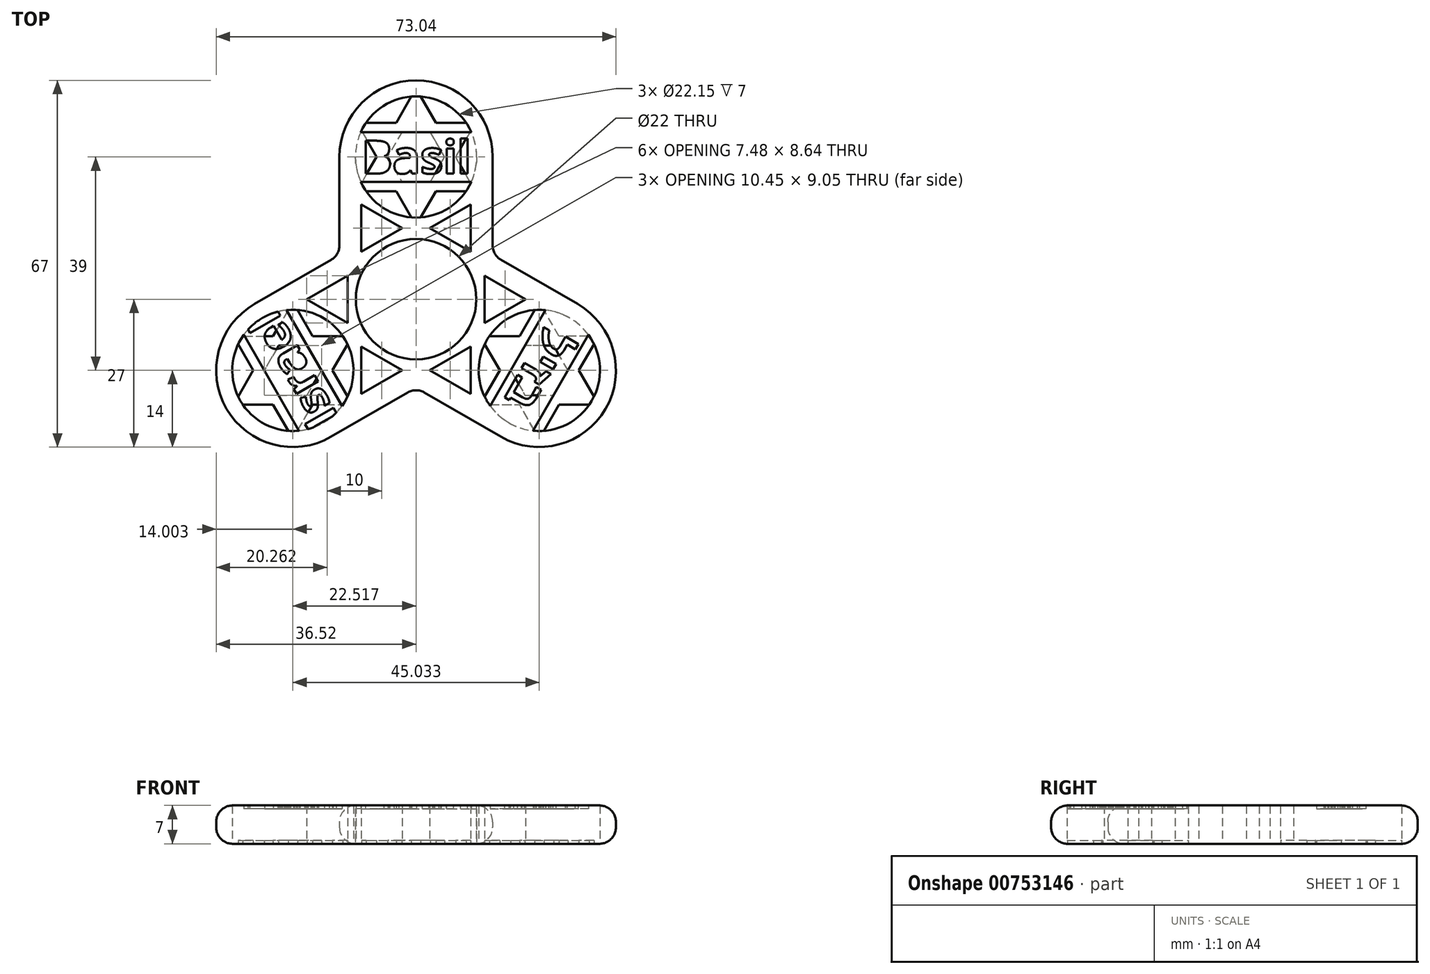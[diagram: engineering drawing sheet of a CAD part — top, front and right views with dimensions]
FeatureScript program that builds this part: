
annotation { "Feature Type Name" : "Feature", "Feature Type Description" : "" }
export const myFeature = defineFeature(function(context is Context, id is Id, definition is map)
    precondition{}
    {
        {
            var Q0;
            Q0=qCreatedBy(makeId("Top.planeOp"),FACE);
            var sketch = newSketch(context, id + "F0", { "sketchPlane" : qUnion([Q0])});
            skCircle(sketch, "E0", {"center": v(0, 0) * mm, "radius": 11 * mm});
            skArc(sketch, "E1", {"start": v(14, 26) * mm, "mid": v(0, 40) * mm, "end": v(-14, 26) * mm});
            skCircle(sketch, "E2.converted", {"center": v(0, 26) * mm, "radius": 11.07 * mm});
            skLineSegment(sketch, "E3", {"start": v(-14, 26) * mm, "end": v(-14, 9.81) * mm});
            skLineSegment(sketch, "E4", {"start": v(14, 26) * mm, "end": v(14, 9.81) * mm});
            skLineSegment(sketch, "E5.0", {"start": v(10, 17.32) * mm, "end": v(10, 8.68) * mm});
            skLineSegment(sketch, "E6", {"start": v(0, 0) * mm, "end": v(14, 8.08) * mm, "construction": true});
            skLineSegment(sketch, "E7", {"start": v(0, 0) * mm, "end": v(0, 26) * mm, "construction": true});
            skLineSegment(sketch, "E8", {"start": v(10, 17.32) * mm, "end": v(2.52, 13) * mm});
            skLineSegment(sketch, "E9", {"start": v(10, 8.68) * mm, "end": v(2.52, 13) * mm});
            skLineSegment(sketch, "E10.anchor1", {"start": v(0, 0) * mm, "end": v(10, 8.68) * mm, "construction": true});
            skPoint(sketch, "E11.visualSharp", {"position": v(14, 8.08) * mm});
            skArc(sketch, "E11.filletArc", {"start": v(14, 9.81) * mm, "mid": v(14.4, 8.31) * mm, "end": v(15.5, 7.22) * mm});
            skLineSegment(sketch, "E12", {"start": v(14, 9.81) * mm, "end": v(17, 9.81) * mm, "construction": true});
            skLineSegment(sketch, "E13", {"start": v(17, 9.81) * mm, "end": v(15.5, 7.22) * mm, "construction": true});
            skArc(sketch, "E14", {"start": v(10, 17.32) * mm, "mid": v(9.28, 13) * mm, "end": v(10, 8.68) * mm, "construction": true});
            skArc(sketch, "E15", {"start": v(2.52, 13) * mm, "mid": v(6.62, 14.53) * mm, "end": v(10, 17.32) * mm, "construction": true});
            skArc(sketch, "E16", {"start": v(10, 17.32) * mm, "mid": v(-6.62, 37.47) * mm, "end": v(2.52, 13) * mm, "construction": true});
            skArc(sketch, "E17", {"start": v(2.52, 13) * mm, "mid": v(-6.62, -11.47) * mm, "end": v(10, 8.68) * mm, "construction": true});
            skArc(sketch, "E18", {"start": v(10, 8.68) * mm, "mid": v(6.62, 11.47) * mm, "end": v(2.52, 13) * mm, "construction": true});
            skLineSegment(sketch, "E19.1.0", {"start": v(-2.52, 13) * mm, "end": v(-10, 8.68) * mm});
            skLineSegment(sketch, "E19.1.1", {"start": v(-10, 17.32) * mm, "end": v(-2.52, 13) * mm});
            skLineSegment(sketch, "E19.1.2", {"start": v(-10, 17.32) * mm, "end": v(-10, 8.68) * mm});
            skLineSegment(sketch, "E19.anchor1", {"start": v(0, 0) * mm, "end": v(2.52, 13) * mm, "construction": true});
            skLineSegment(sketch, "E19.anchor2", {"start": v(0, 0) * mm, "end": v(-10, 8.68) * mm, "construction": true});
            skLineSegment(sketch, "E20.1.0", {"start": v(-10, -8.68) * mm, "end": v(-2.52, -13) * mm});
            skLineSegment(sketch, "E20.1.1", {"start": v(-29.52, -0.88) * mm, "end": v(-15.5, 7.22) * mm});
            skCircle(sketch, "E20.1.2", {"center": v(-22.52, -13) * mm, "radius": 11.07 * mm});
            skArc(sketch, "E20.1.3", {"start": v(-20, 0) * mm, "mid": v(-29.14, -24.47) * mm, "end": v(-12.52, -4.32) * mm, "construction": true});
            skLineSegment(sketch, "E20.1.4", {"start": v(-20, 0) * mm, "end": v(-12.52, 4.32) * mm});
            skArc(sketch, "E20.1.5", {"start": v(-12.52, -4.32) * mm, "mid": v(-15.9, -1.53) * mm, "end": v(-20, 0) * mm, "construction": true});
            skArc(sketch, "E20.1.7", {"start": v(-29.52, -0.88) * mm, "mid": v(-34.64, -20) * mm, "end": v(-15.52, -25.12) * mm});
            skLineSegment(sketch, "E20.1.8", {"start": v(-10, -17.32) * mm, "end": v(-10, -8.68) * mm});
            skLineSegment(sketch, "E20.1.9", {"start": v(-15.5, 7.22) * mm, "end": v(-17, 9.81) * mm, "construction": true});
            skArc(sketch, "E20.1.10", {"start": v(-12.52, 4.32) * mm, "mid": v(-13.24, 0) * mm, "end": v(-12.52, -4.32) * mm, "construction": true});
            skLineSegment(sketch, "E20.1.11", {"start": v(-10, -17.32) * mm, "end": v(-2.52, -13) * mm});
            skLineSegment(sketch, "E20.1.12", {"start": v(-15.52, -25.12) * mm, "end": v(-1.5, -17.03) * mm});
            skArc(sketch, "E20.1.13", {"start": v(-20, 0) * mm, "mid": v(-15.9, 1.53) * mm, "end": v(-12.52, 4.32) * mm, "construction": true});
            skLineSegment(sketch, "E20.1.14", {"start": v(-20, 0) * mm, "end": v(-12.52, -4.32) * mm});
            skPoint(sketch, "E20.1.15", {"position": v(-14, 8.08) * mm});
            skLineSegment(sketch, "E20.1.16", {"start": v(-17, 9.81) * mm, "end": v(-14, 9.81) * mm, "construction": true});
            skLineSegment(sketch, "E20.1.17", {"start": v(-12.52, 4.32) * mm, "end": v(-12.52, -4.32) * mm});
            skArc(sketch, "E20.1.18", {"start": v(-15.5, 7.22) * mm, "mid": v(-14.4, 8.31) * mm, "end": v(-14, 9.81) * mm});
            skLineSegment(sketch, "E20.1.22", {"start": v(0, 0) * mm, "end": v(-12.52, 4.32) * mm, "construction": true});
            skLineSegment(sketch, "E20.1.23", {"start": v(0, 0) * mm, "end": v(-2.52, -13) * mm, "construction": true});
            skLineSegment(sketch, "E20.1.24", {"start": v(0, 0) * mm, "end": v(-12.52, -4.32) * mm, "construction": true});
            skLineSegment(sketch, "E20.1.25", {"start": v(0, 0) * mm, "end": v(-14, 8.08) * mm, "construction": true});
            skLineSegment(sketch, "E20.2.0", {"start": v(12.52, -4.32) * mm, "end": v(12.52, 4.32) * mm});
            skLineSegment(sketch, "E20.2.1", {"start": v(15.52, -25.12) * mm, "end": v(1.5, -17.03) * mm});
            skCircle(sketch, "E20.2.2", {"center": v(22.52, -13) * mm, "radius": 11.07 * mm});
            skArc(sketch, "E20.2.3", {"start": v(10, -17.32) * mm, "mid": v(35.76, -13) * mm, "end": v(10, -8.68) * mm, "construction": true});
            skLineSegment(sketch, "E20.2.4", {"start": v(10, -17.32) * mm, "end": v(2.52, -13) * mm});
            skArc(sketch, "E20.2.5", {"start": v(10, -8.68) * mm, "mid": v(9.28, -13) * mm, "end": v(10, -17.32) * mm, "construction": true});
            skArc(sketch, "E20.2.7", {"start": v(15.52, -25.12) * mm, "mid": v(34.64, -20) * mm, "end": v(29.52, -0.88) * mm});
            skLineSegment(sketch, "E20.2.8", {"start": v(20, 0) * mm, "end": v(12.52, -4.32) * mm});
            skLineSegment(sketch, "E20.2.9", {"start": v(1.5, -17.03) * mm, "end": v(0, -19.63) * mm, "construction": true});
            skArc(sketch, "E20.2.10", {"start": v(2.52, -13) * mm, "mid": v(6.62, -11.47) * mm, "end": v(10, -8.68) * mm, "construction": true});
            skLineSegment(sketch, "E20.2.11", {"start": v(20, 0) * mm, "end": v(12.52, 4.32) * mm});
            skLineSegment(sketch, "E20.2.12", {"start": v(29.52, -0.88) * mm, "end": v(15.5, 7.22) * mm});
            skArc(sketch, "E20.2.13", {"start": v(10, -17.32) * mm, "mid": v(6.62, -14.53) * mm, "end": v(2.52, -13) * mm, "construction": true});
            skLineSegment(sketch, "E20.2.14", {"start": v(10, -17.32) * mm, "end": v(10, -8.68) * mm});
            skPoint(sketch, "E20.2.15", {"position": v(0, -16.17) * mm});
            skLineSegment(sketch, "E20.2.16", {"start": v(0, -19.63) * mm, "end": v(-1.5, -17.03) * mm, "construction": true});
            skLineSegment(sketch, "E20.2.17", {"start": v(2.52, -13) * mm, "end": v(10, -8.68) * mm});
            skArc(sketch, "E20.2.18", {"start": v(1.5, -17.03) * mm, "mid": v(0, -16.63) * mm, "end": v(-1.5, -17.03) * mm});
            skLineSegment(sketch, "E20.2.22", {"start": v(0, 0) * mm, "end": v(2.52, -13) * mm, "construction": true});
            skLineSegment(sketch, "E20.2.23", {"start": v(0, 0) * mm, "end": v(12.52, 4.32) * mm, "construction": true});
            skLineSegment(sketch, "E20.2.24", {"start": v(0, 0) * mm, "end": v(10, -8.68) * mm, "construction": true});
            skLineSegment(sketch, "E20.2.25", {"start": v(0, 0) * mm, "end": v(0, -16.17) * mm, "construction": true});
            skSolve(sketch);
        }
        {
            var Q0;
            Q0=qSketchRegion(id+"F0",true);
            extrude(context, id + "F1", {"entities" : qUnion([Q0]), "depth" : 7 * mm, "offsetDistance" : 25 * mm});
        }
        {
            var Q0;
            Q0=makeQuery(id+"F1.opExtrude","CAP_FACE",FACE,{"disambiguationData":[OSD([sQuery(id+"F0.wireOp",EDGE,"E0"),sQuery(id+"F0.wireOp",EDGE,"E1"),sQuery(id+"F0.wireOp",EDGE,"E2.converted"),sQuery(id+"F0.wireOp",EDGE,"E3"),sQuery(id+"F0.wireOp",EDGE,"E4"),sQuery(id+"F0.wireOp",EDGE,"E5.0"),sQuery(id+"F0.wireOp",EDGE,"E8"),sQuery(id+"F0.wireOp",EDGE,"E9"),sQuery(id+"F0.wireOp",EDGE,"E11.filletArc"),sQuery(id+"F0.wireOp",EDGE,"E19.1.0"),sQuery(id+"F0.wireOp",EDGE,"E19.1.1"),sQuery(id+"F0.wireOp",EDGE,"E19.1.2"),sQuery(id+"F0.wireOp",EDGE,"E20.1.0"),sQuery(id+"F0.wireOp",EDGE,"E20.1.1"),sQuery(id+"F0.wireOp",EDGE,"E20.1.2"),sQuery(id+"F0.wireOp",EDGE,"E20.1.4"),sQuery(id+"F0.wireOp",EDGE,"E20.1.7"),sQuery(id+"F0.wireOp",EDGE,"E20.1.8"),sQuery(id+"F0.wireOp",EDGE,"E20.1.11"),sQuery(id+"F0.wireOp",EDGE,"E20.1.12"),sQuery(id+"F0.wireOp",EDGE,"E20.1.14"),sQuery(id+"F0.wireOp",EDGE,"E20.1.17"),sQuery(id+"F0.wireOp",EDGE,"E20.1.18"),sQuery(id+"F0.wireOp",EDGE,"E20.2.0"),sQuery(id+"F0.wireOp",EDGE,"E20.2.1"),sQuery(id+"F0.wireOp",EDGE,"E20.2.2"),sQuery(id+"F0.wireOp",EDGE,"E20.2.4"),sQuery(id+"F0.wireOp",EDGE,"E20.2.7"),sQuery(id+"F0.wireOp",EDGE,"E20.2.8"),sQuery(id+"F0.wireOp",EDGE,"E20.2.11"),sQuery(id+"F0.wireOp",EDGE,"E20.2.12"),sQuery(id+"F0.wireOp",EDGE,"E20.2.14"),sQuery(id+"F0.wireOp",EDGE,"E20.2.17"),sQuery(id+"F0.wireOp",EDGE,"E20.2.18")])],"isStart":true});
            var sketch = newSketch(context, id + "F2", { "sketchPlane" : qUnion([Q0])});
            skCircle(sketch, "E21", {"center": v(0, -26) * mm, "radius": 12.52 * mm, "construction": true});
            skLineSegment(sketch, "E22", {"start": v(-10.84, -32.26) * mm, "end": v(-3.61, -32.26) * mm});
            skLineSegment(sketch, "E23", {"start": v(10.84, -32.26) * mm, "end": v(7.23, -26) * mm});
            skLineSegment(sketch, "E24", {"start": v(-10.84, -32.26) * mm, "end": v(-7.23, -26) * mm});
            skLineSegment(sketch, "E25", {"start": v(-10.84, -19.74) * mm, "end": v(-3.61, -19.74) * mm});
            skLineSegment(sketch, "E26", {"start": v(10.84, -19.74) * mm, "end": v(7.23, -26) * mm});
            skLineSegment(sketch, "E27", {"start": v(0, -38.52) * mm, "end": v(-3.61, -32.26) * mm});
            skCircle(sketch, "E28.cCircle", {"center": v(0, -26) * mm, "radius": 4.53 * mm, "construction": true});
            skLineSegment(sketch, "E28.0", {"start": v(-5.23, -26) * mm, "end": v(-2.61, -21.47) * mm});
            skLineSegment(sketch, "E28.1", {"start": v(-2.61, -21.47) * mm, "end": v(2.61, -21.47) * mm});
            skLineSegment(sketch, "E28.2", {"start": v(2.61, -21.47) * mm, "end": v(5.23, -26) * mm});
            skLineSegment(sketch, "E28.3", {"start": v(5.23, -26) * mm, "end": v(2.61, -30.53) * mm});
            skLineSegment(sketch, "E28.4", {"start": v(2.61, -30.53) * mm, "end": v(-2.61, -30.53) * mm});
            skLineSegment(sketch, "E28.5", {"start": v(-2.61, -30.53) * mm, "end": v(-5.23, -26) * mm});
            skPoint(sketch, "E28.0.midPoint", {"position": v(-3.92, -23.74) * mm});
            skLineSegment(sketch, "E29.trimOffspring", {"start": v(3.61, -19.74) * mm, "end": v(10.84, -19.74) * mm});
            skLineSegment(sketch, "E30.trimOffspring", {"start": v(-3.61, -19.74) * mm, "end": v(0, -13.48) * mm});
            skLineSegment(sketch, "E31.trimOffspring", {"start": v(-7.23, -26) * mm, "end": v(-10.84, -19.74) * mm});
            skLineSegment(sketch, "E32.trimOffspring", {"start": v(3.61, -32.26) * mm, "end": v(10.84, -32.26) * mm});
            skLineSegment(sketch, "E33.trimOffspring", {"start": v(3.61, -32.26) * mm, "end": v(0, -38.52) * mm});
            skLineSegment(sketch, "E34.trimOffspring", {"start": v(3.61, -19.74) * mm, "end": v(0, -13.48) * mm});
            skLineSegment(sketch, "E35.1.0", {"start": v(15.3, 13) * mm, "end": v(11.68, 19.26) * mm});
            skLineSegment(sketch, "E35.1.1", {"start": v(25.13, 17.53) * mm, "end": v(27.74, 13) * mm});
            skLineSegment(sketch, "E35.1.2", {"start": v(22.52, 25.52) * mm, "end": v(18.9, 19.26) * mm});
            skLineSegment(sketch, "E35.1.3", {"start": v(18.9, 6.74) * mm, "end": v(11.68, 6.74) * mm});
            skLineSegment(sketch, "E35.1.4", {"start": v(22.52, 0.48) * mm, "end": v(18.9, 6.74) * mm});
            skCircle(sketch, "E35.1.5", {"center": v(22.52, 13) * mm, "radius": 12.52 * mm, "construction": true});
            skLineSegment(sketch, "E35.1.6", {"start": v(26.13, 19.26) * mm, "end": v(33.36, 19.26) * mm});
            skLineSegment(sketch, "E35.1.7", {"start": v(15.3, 13) * mm, "end": v(11.68, 6.74) * mm});
            skLineSegment(sketch, "E35.1.8", {"start": v(19.9, 8.47) * mm, "end": v(17.3, 13) * mm});
            skLineSegment(sketch, "E35.1.9", {"start": v(26.13, 19.26) * mm, "end": v(22.52, 25.52) * mm});
            skLineSegment(sketch, "E35.1.10", {"start": v(11.68, 19.26) * mm, "end": v(18.9, 19.26) * mm});
            skLineSegment(sketch, "E35.1.11", {"start": v(33.36, 6.74) * mm, "end": v(29.74, 13) * mm});
            skLineSegment(sketch, "E35.1.12", {"start": v(19.9, 17.53) * mm, "end": v(25.13, 17.53) * mm});
            skLineSegment(sketch, "E35.1.13", {"start": v(33.36, 6.74) * mm, "end": v(26.13, 6.74) * mm});
            skPoint(sketch, "E35.1.14", {"position": v(22.52, 8.47) * mm});
            skLineSegment(sketch, "E35.1.15", {"start": v(26.13, 6.74) * mm, "end": v(22.52, 0.48) * mm});
            skLineSegment(sketch, "E35.1.16", {"start": v(27.74, 13) * mm, "end": v(25.13, 8.47) * mm});
            skLineSegment(sketch, "E35.1.17", {"start": v(33.36, 19.26) * mm, "end": v(29.74, 13) * mm});
            skLineSegment(sketch, "E35.1.18", {"start": v(17.3, 13) * mm, "end": v(19.9, 17.53) * mm});
            skCircle(sketch, "E35.1.19", {"center": v(22.52, 13) * mm, "radius": 4.53 * mm, "construction": true});
            skLineSegment(sketch, "E35.1.20", {"start": v(25.13, 8.47) * mm, "end": v(19.9, 8.47) * mm});
            skLineSegment(sketch, "E35.2.0", {"start": v(-18.9, 6.74) * mm, "end": v(-22.52, 0.48) * mm});
            skLineSegment(sketch, "E35.2.1", {"start": v(-27.74, 13) * mm, "end": v(-25.13, 17.53) * mm});
            skLineSegment(sketch, "E35.2.2", {"start": v(-33.36, 6.74) * mm, "end": v(-26.13, 6.74) * mm});
            skLineSegment(sketch, "E35.2.3", {"start": v(-15.3, 13) * mm, "end": v(-11.68, 6.74) * mm});
            skLineSegment(sketch, "E35.2.4", {"start": v(-11.68, 19.26) * mm, "end": v(-15.3, 13) * mm});
            skCircle(sketch, "E35.2.5", {"center": v(-22.52, 13) * mm, "radius": 12.52 * mm, "construction": true});
            skLineSegment(sketch, "E35.2.6", {"start": v(-29.74, 13) * mm, "end": v(-33.36, 19.26) * mm});
            skLineSegment(sketch, "E35.2.7", {"start": v(-18.9, 6.74) * mm, "end": v(-11.68, 6.74) * mm});
            skLineSegment(sketch, "E35.2.8", {"start": v(-17.3, 13) * mm, "end": v(-19.9, 8.47) * mm});
            skLineSegment(sketch, "E35.2.9", {"start": v(-29.74, 13) * mm, "end": v(-33.36, 6.74) * mm});
            skLineSegment(sketch, "E35.2.10", {"start": v(-22.52, 0.48) * mm, "end": v(-26.13, 6.74) * mm});
            skLineSegment(sketch, "E35.2.11", {"start": v(-22.52, 25.52) * mm, "end": v(-26.13, 19.26) * mm});
            skLineSegment(sketch, "E35.2.12", {"start": v(-25.13, 8.47) * mm, "end": v(-27.74, 13) * mm});
            skLineSegment(sketch, "E35.2.13", {"start": v(-22.52, 25.52) * mm, "end": v(-18.9, 19.26) * mm});
            skPoint(sketch, "E35.2.14", {"position": v(-18.6, 15.26) * mm});
            skLineSegment(sketch, "E35.2.15", {"start": v(-18.9, 19.26) * mm, "end": v(-11.68, 19.26) * mm});
            skLineSegment(sketch, "E35.2.16", {"start": v(-25.13, 17.53) * mm, "end": v(-19.9, 17.53) * mm});
            skLineSegment(sketch, "E35.2.17", {"start": v(-33.36, 19.26) * mm, "end": v(-26.13, 19.26) * mm});
            skLineSegment(sketch, "E35.2.18", {"start": v(-19.9, 8.47) * mm, "end": v(-25.13, 8.47) * mm});
            skCircle(sketch, "E35.2.19", {"center": v(-22.52, 13) * mm, "radius": 4.53 * mm, "construction": true});
            skLineSegment(sketch, "E35.2.20", {"start": v(-19.9, 17.53) * mm, "end": v(-17.3, 13) * mm});
            skPoint(sketch, "E35.center", {"position": v(0, 0) * mm});
            skSolve(sketch);
        }
        {
            var Q0;
            Q0 = qSketchRegion(id + "F2", true);
            extrude(context, id + "F3", {"entities" : qUnion([Q0]), "operationType" : NewBodyOperationType.ADD, "oppositeDirection" : true, "depth" : 0.6 * mm, "offsetDistance" : 25 * mm});
        }
        {
            var Q0;
            Q0=makeQuery(id+"F1.opExtrude","CAP_FACE",FACE,{"disambiguationData":[OSD([sQuery(id+"F0.wireOp",EDGE,"E0"),sQuery(id+"F0.wireOp",EDGE,"E1"),sQuery(id+"F0.wireOp",EDGE,"E2.converted"),sQuery(id+"F0.wireOp",EDGE,"E3"),sQuery(id+"F0.wireOp",EDGE,"E4"),sQuery(id+"F0.wireOp",EDGE,"E5.0"),sQuery(id+"F0.wireOp",EDGE,"E8"),sQuery(id+"F0.wireOp",EDGE,"E9"),sQuery(id+"F0.wireOp",EDGE,"E11.filletArc"),sQuery(id+"F0.wireOp",EDGE,"E19.1.0"),sQuery(id+"F0.wireOp",EDGE,"E19.1.1"),sQuery(id+"F0.wireOp",EDGE,"E19.1.2"),sQuery(id+"F0.wireOp",EDGE,"E20.1.0"),sQuery(id+"F0.wireOp",EDGE,"E20.1.1"),sQuery(id+"F0.wireOp",EDGE,"E20.1.2"),sQuery(id+"F0.wireOp",EDGE,"E20.1.4"),sQuery(id+"F0.wireOp",EDGE,"E20.1.7"),sQuery(id+"F0.wireOp",EDGE,"E20.1.8"),sQuery(id+"F0.wireOp",EDGE,"E20.1.11"),sQuery(id+"F0.wireOp",EDGE,"E20.1.12"),sQuery(id+"F0.wireOp",EDGE,"E20.1.14"),sQuery(id+"F0.wireOp",EDGE,"E20.1.17"),sQuery(id+"F0.wireOp",EDGE,"E20.1.18"),sQuery(id+"F0.wireOp",EDGE,"E20.2.0"),sQuery(id+"F0.wireOp",EDGE,"E20.2.1"),sQuery(id+"F0.wireOp",EDGE,"E20.2.2"),sQuery(id+"F0.wireOp",EDGE,"E20.2.4"),sQuery(id+"F0.wireOp",EDGE,"E20.2.7"),sQuery(id+"F0.wireOp",EDGE,"E20.2.8"),sQuery(id+"F0.wireOp",EDGE,"E20.2.11"),sQuery(id+"F0.wireOp",EDGE,"E20.2.12"),sQuery(id+"F0.wireOp",EDGE,"E20.2.14"),sQuery(id+"F0.wireOp",EDGE,"E20.2.17"),sQuery(id+"F0.wireOp",EDGE,"E20.2.18")])],"isStart":false});
            var sketch = newSketch(context, id + "F4", { "sketchPlane" : qUnion([Q0])});
            skLineSegment(sketch, "E36", {"start": v(-11.67, 30.53) * mm, "end": v(11.67, 30.53) * mm});
            skText(sketch, "E37", { "text": "Basil", "fontName": "OpenSans-Bold.ttf"});
            skPoint(sketch, "E38.center", {"position": v(0, 0) * mm});
            skText(sketch, "E39", { "text": "ליזב", "fontName": "Arimo-Bold.ttf"});
            skText(sketch, "E40", { "text": "Israel", "fontName": "OpenSans-Bold.ttf"});
            skLineSegment(sketch, "E41", {"start": v(-11.67, 21.47) * mm, "end": v(11.67, 21.47) * mm});
            skArc(sketch, "E42", {"start": v(-11.67, 30.53) * mm, "mid": v(-12.52, 26) * mm, "end": v(-11.67, 21.47) * mm});
            skArc(sketch, "E43", {"start": v(11.67, 21.47) * mm, "mid": v(12.52, 26) * mm, "end": v(11.67, 30.53) * mm});
            skLineSegment(sketch, "E44.1.0", {"start": v(-20.6, -25.37) * mm, "end": v(-32.27, -5.16) * mm});
            skArc(sketch, "E44.1.1", {"start": v(-20.6, -25.37) * mm, "mid": v(-16.26, -23.84) * mm, "end": v(-12.76, -20.84) * mm});
            skLineSegment(sketch, "E44.1.2", {"start": v(-12.76, -20.84) * mm, "end": v(-24.43, -0.63) * mm});
            skArc(sketch, "E44.1.3", {"start": v(-24.43, -0.63) * mm, "mid": v(-28.77, -2.16) * mm, "end": v(-32.27, -5.16) * mm});
            skLineSegment(sketch, "E44.2.0", {"start": v(32.27, -5.16) * mm, "end": v(20.6, -25.37) * mm});
            skArc(sketch, "E44.2.1", {"start": v(32.27, -5.16) * mm, "mid": v(28.77, -2.16) * mm, "end": v(24.43, -0.63) * mm});
            skLineSegment(sketch, "E44.2.2", {"start": v(24.43, -0.63) * mm, "end": v(12.76, -20.84) * mm});
            skArc(sketch, "E44.2.3", {"start": v(12.76, -20.84) * mm, "mid": v(16.26, -23.84) * mm, "end": v(20.6, -25.37) * mm});
            skPoint(sketch, "E45", {"position": v(18.6, -10.74) * mm});
            skPoint(sketch, "E46", {"position": v(-18.6, -10.74) * mm});
            const initialGuessF4  = {"E37": [-0.00996, 0.02297, 1, 0, 0.00605], "E39": [0.02392, -0.00452, -0.5, -0.86603, 0.00605], "E40": [-0.01408, -0.02157, -0.5, 0.86603, 0.00605]};
            skSetInitialGuess(sketch, initialGuessF4);
            skSolve(sketch);
        }
        {
            var Q0;
            Q0 = qSketchRegion(id + "F4", true);
            extrude(context, id + "F5", {"entities" : qUnion([Q0]), "operationType" : NewBodyOperationType.ADD, "oppositeDirection" : true, "depth" : 0.6 * mm, "offsetDistance" : 25 * mm});
        }
        {
            var Q0;
            Q0=makeQuery(id+"F1.opExtrude","CAP_EDGE",EDGE,{"disambiguationData":[OSD([sQuery(id+"F0.wireOp",EDGE,"E1")])],"isStart":false});
            var Q1;
            Q1=makeQuery(id+"F1.opExtrude","CAP_EDGE",EDGE,{"disambiguationData":[OSD([sQuery(id+"F0.wireOp",EDGE,"E1")])],"isStart":true});
            fillet(context, id + "F6", {"entities" : qUnion([Q0, Q1]), "radius" : 3 * mm, "tangentPropagation" : true, "allowEdgeOverflow" : false});
        }
    });
